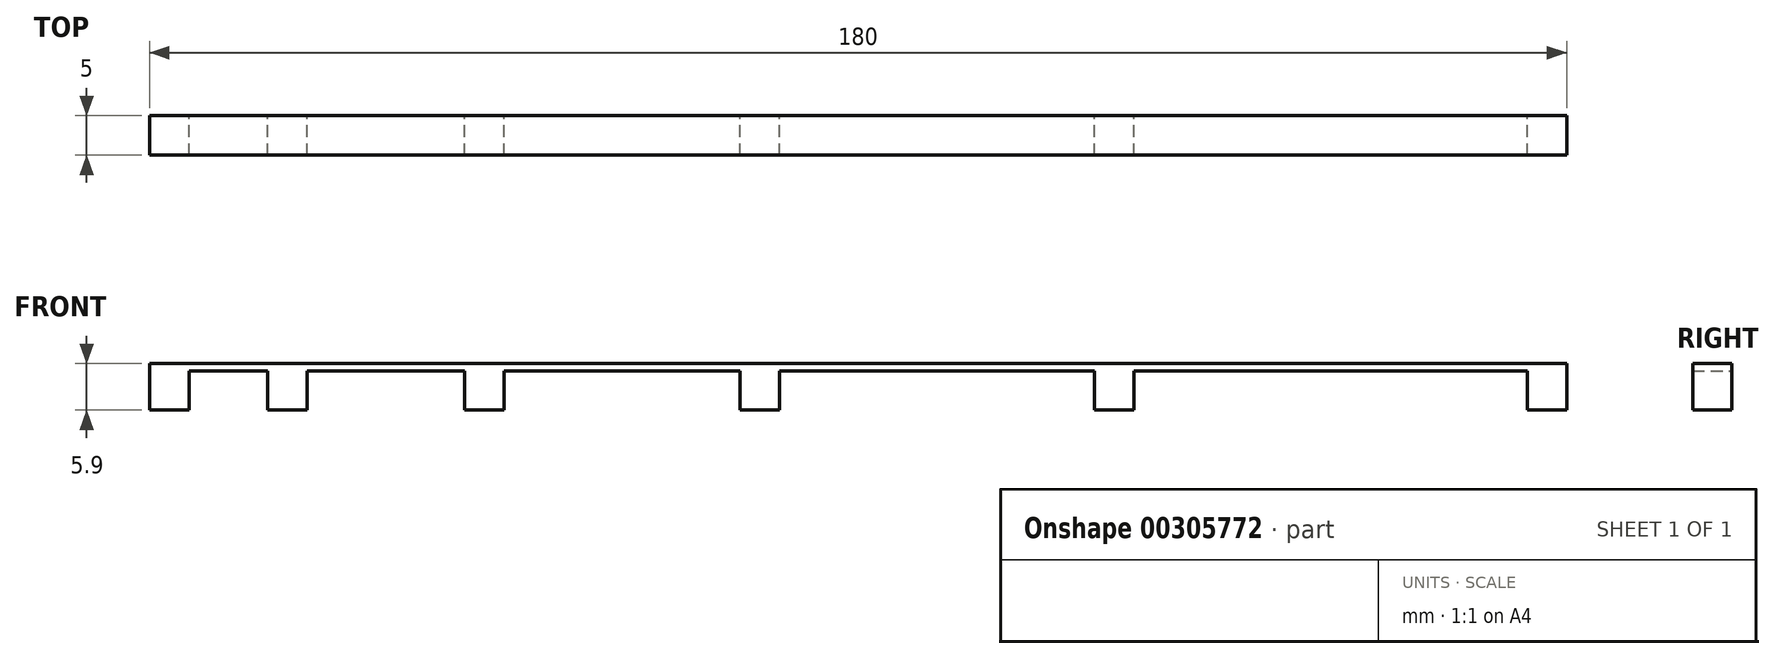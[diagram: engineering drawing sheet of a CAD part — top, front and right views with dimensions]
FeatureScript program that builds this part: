
annotation { "Feature Type Name" : "Feature", "Feature Type Description" : "" }
export const myFeature = defineFeature(function(context is Context, id is Id, definition is map)
    precondition{}
    {
        {
            var Q0;
            Q0=qCreatedBy(makeId("Top.planeOp"),FACE);
            var sketch = newSketch(context, id + "F0", { "sketchPlane" : qUnion([Q0])});
            skLineSegment(sketch, "E0.bottom", {"start": v(0, 0) * mm, "end": v(5, 0) * mm});
            skLineSegment(sketch, "E0.top", {"start": v(0, 5) * mm, "end": v(5, 5) * mm});
            skLineSegment(sketch, "E0.left", {"start": v(0, 0) * mm, "end": v(0, 5) * mm});
            skLineSegment(sketch, "E0.right", {"start": v(5, 0) * mm, "end": v(5, 5) * mm});
            skSolve(sketch);
        }
        {
            var Q0;
            Q0=makeQuery(id+"F0.imprint","IMPRINT",FACE,{"disambiguationData":[TD([[makeQuery(id+"F0.imprint","IMPRINT",EDGE,{"derivedFrom":sQuery(id+"F0.wireOp",EDGE,"E0.bottom")}),1.0]])]});
            extrude(context, id + "F1", {"entities" : qUnion([Q0]), "depth" : 5 * mm});
        }
        {
            var Q0;
            Q0=makeQuery(id+"F1.opExtrude","SWEPT_BODY",BODY,{"disambiguationData":[OSD([sQuery(id+"F0.wireOp",EDGE,"E0.bottom"),sQuery(id+"F0.wireOp",EDGE,"E0.top"),sQuery(id+"F0.wireOp",EDGE,"E0.left"),sQuery(id+"F0.wireOp",EDGE,"E0.right")])]});
            transform(context, id + "F2", {"entities" : qUnion([Q0]), "transformType" : TransformType.TRANSLATION_3D, "dx" : 15 * mm, "dy" : 0 * mm, "dz" : 0 * mm, "makeCopy" : true});
        }
        {
            var Q0;
            Q0=makeQuery(id+"F2.opPattern","COPY",BODY,{"derivedFrom":makeQuery(id+"F1.opExtrude","SWEPT_BODY",BODY,{"disambiguationData":[OSD([sQuery(id+"F0.wireOp",EDGE,"E0.bottom"),sQuery(id+"F0.wireOp",EDGE,"E0.top"),sQuery(id+"F0.wireOp",EDGE,"E0.left"),sQuery(id+"F0.wireOp",EDGE,"E0.right")])]}),"instanceName":"1"});
            transform(context, id + "F3", {"entities" : qUnion([Q0]), "transformType" : TransformType.TRANSLATION_3D, "dx" : 25 * mm, "dy" : 0 * mm, "dz" : 0 * mm, "makeCopy" : true});
        }
        {
            var Q0;
            Q0=makeQuery(id+"F3.opPattern","COPY",BODY,{"derivedFrom":makeQuery(id+"F2.opPattern","COPY",BODY,{"derivedFrom":makeQuery(id+"F1.opExtrude","SWEPT_BODY",BODY,{"disambiguationData":[OSD([sQuery(id+"F0.wireOp",EDGE,"E0.bottom"),sQuery(id+"F0.wireOp",EDGE,"E0.top"),sQuery(id+"F0.wireOp",EDGE,"E0.left"),sQuery(id+"F0.wireOp",EDGE,"E0.right")])]}),"instanceName":"1"}),"instanceName":"1"});
            transform(context, id + "F4", {"entities" : qUnion([Q0]), "transformType" : TransformType.TRANSLATION_3D, "dx" : 35 * mm, "dy" : 0 * mm, "dz" : 0 * mm, "makeCopy" : true});
        }
        {
            var Q0;
            Q0=makeQuery(id+"F4.opPattern","COPY",BODY,{"derivedFrom":makeQuery(id+"F3.opPattern","COPY",BODY,{"derivedFrom":makeQuery(id+"F2.opPattern","COPY",BODY,{"derivedFrom":makeQuery(id+"F1.opExtrude","SWEPT_BODY",BODY,{"disambiguationData":[OSD([sQuery(id+"F0.wireOp",EDGE,"E0.bottom"),sQuery(id+"F0.wireOp",EDGE,"E0.top"),sQuery(id+"F0.wireOp",EDGE,"E0.left"),sQuery(id+"F0.wireOp",EDGE,"E0.right")])]}),"instanceName":"1"}),"instanceName":"1"}),"instanceName":"1"});
            transform(context, id + "F5", {"entities" : qUnion([Q0]), "transformType" : TransformType.TRANSLATION_3D, "dx" : 45 * mm, "dy" : 0 * mm, "dz" : 0 * mm, "makeCopy" : true});
        }
        {
            var Q0;
            Q0=makeQuery(id+"F5.opPattern","COPY",BODY,{"derivedFrom":makeQuery(id+"F4.opPattern","COPY",BODY,{"derivedFrom":makeQuery(id+"F3.opPattern","COPY",BODY,{"derivedFrom":makeQuery(id+"F2.opPattern","COPY",BODY,{"derivedFrom":makeQuery(id+"F1.opExtrude","SWEPT_BODY",BODY,{"disambiguationData":[OSD([sQuery(id+"F0.wireOp",EDGE,"E0.bottom"),sQuery(id+"F0.wireOp",EDGE,"E0.top"),sQuery(id+"F0.wireOp",EDGE,"E0.left"),sQuery(id+"F0.wireOp",EDGE,"E0.right")])]}),"instanceName":"1"}),"instanceName":"1"}),"instanceName":"1"}),"instanceName":"1"});
            transform(context, id + "F6", {"entities" : qUnion([Q0]), "transformType" : TransformType.TRANSLATION_3D, "dx" : 55 * mm, "dy" : 0 * mm, "dz" : 0 * mm, "makeCopy" : true});
        }
        {
            var Q0;
            Q0=makeQuery(id+"F1.opExtrude","CAP_FACE",FACE,{"disambiguationData":[OSD([sQuery(id+"F0.wireOp",EDGE,"E0.bottom"),sQuery(id+"F0.wireOp",EDGE,"E0.top"),sQuery(id+"F0.wireOp",EDGE,"E0.left"),sQuery(id+"F0.wireOp",EDGE,"E0.right")])],"isStart":false});
            var sketch = newSketch(context, id + "F7", { "sketchPlane" : qUnion([Q0])});
            skPoint(sketch, "E1.0", {"position": v(180, 5) * mm});
            skLineSegment(sketch, "E2.bottom", {"start": v(0, 0) * mm, "end": v(180, 0) * mm});
            skLineSegment(sketch, "E2.top", {"start": v(0, 5) * mm, "end": v(180, 5) * mm});
            skLineSegment(sketch, "E2.left", {"start": v(0, 0) * mm, "end": v(0, 5) * mm});
            skLineSegment(sketch, "E2.right", {"start": v(180, 0) * mm, "end": v(180, 5) * mm});
            skSolve(sketch);
        }
        {
            var Q0;
            {var subQ2=sQuery(id+"F7.wireOp",EDGE,"E2.right");Q0=makeQuery(id+"F7.imprint","IMPRINT",FACE,{"disambiguationData":[TD([[makeQuery(id+"F7.imprint","IMPRINT",EDGE,{"derivedFrom":subQ2}),1.0]])]});}
            var Q1;
            {var subQ0=sQuery(id+"F7.wireOp",EDGE,"E2.left");Q1=makeQuery(id+"F7.imprint","IMPRINT",FACE,{"disambiguationData":[TD([[makeQuery(id+"F7.imprint","IMPRINT",EDGE,{"derivedFrom":subQ0}),-1.0]])]});}
            extrude(context, id + "F8", {"entities" : qUnion([Q0, Q1]), "operationType" : NewBodyOperationType.ADD, "depth" : 0.9 * mm});
        }
    });
